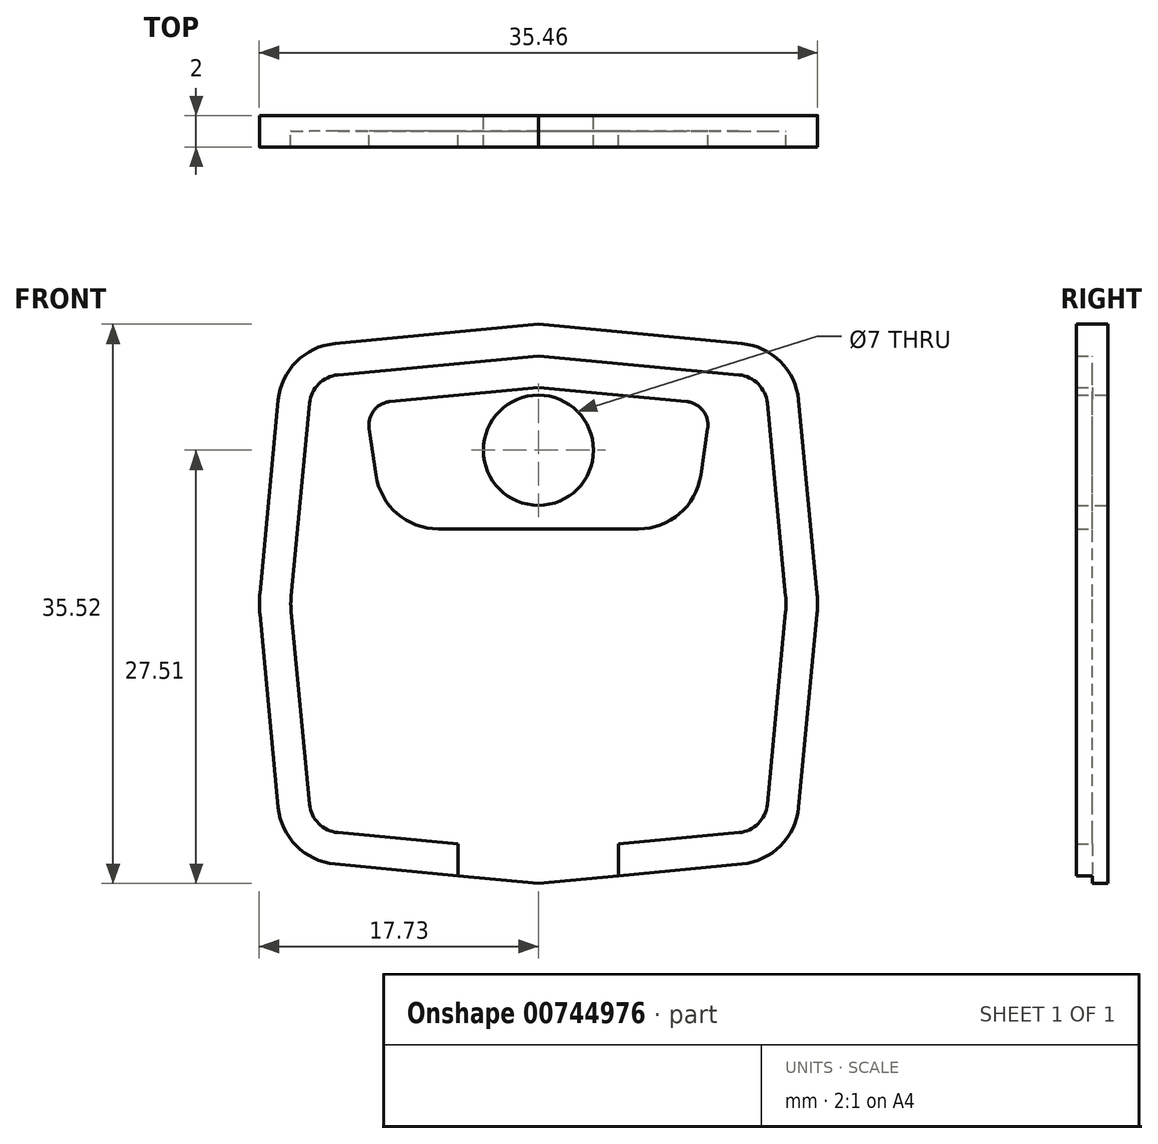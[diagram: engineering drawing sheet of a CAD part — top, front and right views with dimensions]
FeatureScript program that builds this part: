
annotation { "Feature Type Name" : "Feature", "Feature Type Description" : "" }
export const myFeature = defineFeature(function(context is Context, id is Id, definition is map)
    precondition{}
    {
        {
            var Q0;
            Q0=qCreatedBy(makeId("Front.planeOp"),FACE);
            var sketch = newSketch(context, id + "F0", { "sketchPlane" : qUnion([Q0])});
            skLineSegment(sketch, "E0.bottom", {"start": v(0, 31.5) * mm, "end": v(31.5, 31.5) * mm, "construction": true});
            skLineSegment(sketch, "E0.top", {"start": v(0, 0) * mm, "end": v(31.5, 0) * mm, "construction": true});
            skLineSegment(sketch, "E0.left", {"start": v(0, 31.5) * mm, "end": v(0, 0) * mm, "construction": true});
            skLineSegment(sketch, "E0.right", {"start": v(31.5, 31.5) * mm, "end": v(31.5, 0) * mm, "construction": true});
            skLineSegment(sketch, "E1", {"start": v(15.75, 31.5) * mm, "end": v(15.75, 0) * mm, "construction": true});
            skPoint(sketch, "E2", {"position": v(0, 30) * mm});
            skPoint(sketch, "E3", {"position": v(0, 1.5) * mm});
            skPoint(sketch, "E4", {"position": v(15.75, 20.5) * mm});
            skPoint(sketch, "E5", {"position": v(1.5, 31.5) * mm});
            skPoint(sketch, "E6", {"position": v(1.5, 0) * mm});
            skPoint(sketch, "E7", {"position": v(0, 15.75) * mm});
            skLineSegment(sketch, "E8", {"start": v(1.5, 31.5) * mm, "end": v(0, 15.75) * mm, "construction": true});
            skLineSegment(sketch, "E9", {"start": v(1.5, 0) * mm, "end": v(0, 15.75) * mm, "construction": true});
            skLineSegment(sketch, "E10", {"start": v(0, 30) * mm, "end": v(15.75, 31.5) * mm, "construction": true});
            skLineSegment(sketch, "E11", {"start": v(0, 1.5) * mm, "end": v(15.75, 0) * mm, "construction": true});
            skLineSegment(sketch, "E12", {"start": v(15.75, 20.5) * mm, "end": v(0, 20.5) * mm, "construction": true});
            skLineSegment(sketch, "E13", {"start": v(-1.54, 27.84) * mm, "end": v(18.15, 29.72) * mm, "construction": true});
            skLineSegment(sketch, "E14", {"start": v(5, 26.88) * mm, "end": v(5.44, 23.91) * mm});
            skLineSegment(sketch, "E15", {"start": v(6.34, 28.6) * mm, "end": v(15.75, 29.5) * mm});
            skLineSegment(sketch, "E16", {"start": v(15.75, 20.5) * mm, "end": v(9.4, 20.5) * mm});
            skArc(sketch, "E17", {"start": v(6.34, 28.6) * mm, "mid": v(5.3, 28.03) * mm, "end": v(5, 26.88) * mm});
            skArc(sketch, "E18", {"start": v(5.44, 23.91) * mm, "mid": v(6.78, 21.47) * mm, "end": v(9.4, 20.5) * mm});
            skLineSegment(sketch, "E19", {"start": v(15.75, 31.5) * mm, "end": v(3.01, 30.29) * mm});
            skLineSegment(sketch, "E20", {"start": v(1.21, 28.49) * mm, "end": v(0.05, 16.22) * mm, "construction": true});
            skLineSegment(sketch, "E21", {"start": v(0.05, 15.28) * mm, "end": v(1.21, 3.01) * mm});
            skLineSegment(sketch, "E22", {"start": v(3.01, 1.21) * mm, "end": v(15.75, 0) * mm});
            skArc(sketch, "E23", {"start": v(3.01, 30.29) * mm, "mid": v(1.79, 29.71) * mm, "end": v(1.21, 28.49) * mm});
            skArc(sketch, "E24", {"start": v(0.05, 16.22) * mm, "mid": v(0.02, 15.75) * mm, "end": v(0.05, 15.28) * mm});
            skArc(sketch, "E25", {"start": v(1.21, 3.01) * mm, "mid": v(1.79, 1.79) * mm, "end": v(3.01, 1.21) * mm});
            skLineSegment(sketch, "E26", {"start": v(1.21, 28.49) * mm, "end": v(0.05, 16.22) * mm});
            skArc(sketch, "E27.MirrorCS", {"start": v(28.49, 30.29) * mm, "mid": v(29.71, 29.71) * mm, "end": v(30.29, 28.49) * mm});
            skArc(sketch, "E28.MirrorCS", {"start": v(25.16, 28.6) * mm, "mid": v(26.2, 28.03) * mm, "end": v(26.5, 26.88) * mm});
            skArc(sketch, "E29.MirrorCS", {"start": v(26.06, 23.91) * mm, "mid": v(24.72, 21.47) * mm, "end": v(22.1, 20.5) * mm});
            skArc(sketch, "E30.MirrorCS", {"start": v(30.29, 3.01) * mm, "mid": v(29.71, 1.79) * mm, "end": v(28.49, 1.21) * mm});
            skArc(sketch, "E31.MirrorCS", {"start": v(31.45, 16.22) * mm, "mid": v(31.48, 15.75) * mm, "end": v(31.45, 15.28) * mm});
            skLineSegment(sketch, "E32.MirrorCS", {"start": v(26.5, 26.88) * mm, "end": v(26.06, 23.91) * mm});
            skLineSegment(sketch, "E33.MirrorCS", {"start": v(28.49, 1.21) * mm, "end": v(15.75, 0) * mm});
            skLineSegment(sketch, "E34.MirrorCS", {"start": v(30.29, 28.49) * mm, "end": v(31.45, 16.22) * mm});
            skLineSegment(sketch, "E35.MirrorCS", {"start": v(31.45, 15.28) * mm, "end": v(30.29, 3.01) * mm});
            skLineSegment(sketch, "E36.MirrorCS", {"start": v(15.75, 31.5) * mm, "end": v(28.49, 30.29) * mm});
            skLineSegment(sketch, "E37.MirrorCS", {"start": v(25.16, 28.6) * mm, "end": v(15.75, 29.5) * mm});
            skLineSegment(sketch, "E38.MirrorCS", {"start": v(15.75, 20.5) * mm, "end": v(22.1, 20.5) * mm});
            skCircle(sketch, "E39", {"center": v(15.75, 25.5) * mm, "radius": 3.5 * mm});
            skLineSegment(sketch, "E40.0", {"start": v(28.68, -0.78) * mm, "end": v(15.75, -2) * mm});
            skArc(sketch, "E41.0", {"start": v(32.28, 2.82) * mm, "mid": v(31.12, 0.38) * mm, "end": v(28.68, -0.78) * mm});
            skLineSegment(sketch, "E42.0", {"start": v(33.45, 15.09) * mm, "end": v(32.28, 2.82) * mm});
            skArc(sketch, "E43.0", {"start": v(33.45, 16.41) * mm, "mid": v(33.48, 15.75) * mm, "end": v(33.45, 15.09) * mm});
            skLineSegment(sketch, "E44.0", {"start": v(32.28, 28.68) * mm, "end": v(33.45, 16.41) * mm});
            skArc(sketch, "E45.0", {"start": v(28.68, 32.28) * mm, "mid": v(31.12, 31.12) * mm, "end": v(32.28, 28.68) * mm});
            skLineSegment(sketch, "E46.0", {"start": v(15.75, 33.5) * mm, "end": v(28.68, 32.28) * mm});
            skLineSegment(sketch, "E47.MirrorCS", {"start": v(15.75, 33.5) * mm, "end": v(2.82, 32.28) * mm});
            skArc(sketch, "E48.MirrorCS", {"start": v(2.82, 32.28) * mm, "mid": v(0.38, 31.12) * mm, "end": v(-0.78, 28.68) * mm});
            skLineSegment(sketch, "E49.MirrorCS", {"start": v(-0.78, 28.68) * mm, "end": v(-1.95, 16.41) * mm});
            skArc(sketch, "E50.MirrorCS", {"start": v(-1.95, 16.41) * mm, "mid": v(-1.98, 15.75) * mm, "end": v(-1.95, 15.09) * mm});
            skLineSegment(sketch, "E51.MirrorCS", {"start": v(-1.95, 15.09) * mm, "end": v(-0.78, 2.82) * mm});
            skArc(sketch, "E52.MirrorCS", {"start": v(-0.78, 2.82) * mm, "mid": v(0.38, 0.38) * mm, "end": v(2.82, -0.78) * mm});
            skLineSegment(sketch, "E53.MirrorCS", {"start": v(2.82, -0.78) * mm, "end": v(15.75, -2) * mm});
            skLineSegment(sketch, "E54.left", {"start": v(10.65, -1.52) * mm, "end": v(10.65, 0.49) * mm});
            skLineSegment(sketch, "E54.right", {"start": v(20.85, -1.52) * mm, "end": v(20.85, 0.49) * mm});
            skSolve(sketch);
        }
        {
            var Q0;
            Q0=makeQuery(id+"F0.imprint","IMPRINT",FACE,{"disambiguationData":[TD([[makeQuery(id+"F0.imprint","IMPRINT",EDGE,{"derivedFrom":sQuery(id+"F0.wireOp",EDGE,"E19")}),-1.0]])]});
            var Q1;
            Q1=makeQuery(id+"F0.imprint","IMPRINT",FACE,{"disambiguationData":[TD([[makeQuery(id+"F0.imprint","IMPRINT",EDGE,{"derivedFrom":sQuery(id+"F0.wireOp",EDGE,"E14")}),-1.0]])]});
            var Q2;
            Q2=makeQuery(id+"F0.imprint","IMPRINT",FACE,{"disambiguationData":[TD([[makeQuery(id+"F0.imprint","IMPRINT",EDGE,{"derivedFrom":sQuery(id+"F0.wireOp",EDGE,"E14")}),1.0]])]});
            var Q3;
            {var subQ3=sQuery(id+"F0.wireOp",EDGE,"E54.left");Q3=makeQuery(id+"F0.imprint","IMPRINT",FACE,{"disambiguationData":[TD([[makeQuery(id+"F0.imprint","IMPRINT",EDGE,{"derivedFrom":subQ3}),-1.0]])]});}
            extrude(context, id + "F1", {"entities" : qUnion([Q0, Q1, Q2, Q3]), "depth" : 1 * mm, "offsetDistance" : 25 * mm});
        }
        {
            var Q0;
            Q0=makeQuery(id+"F0.imprint","IMPRINT",FACE,{"disambiguationData":[TD([[makeQuery(id+"F0.imprint","IMPRINT",EDGE,{"derivedFrom":sQuery(id+"F0.wireOp",EDGE,"E14")}),1.0]])]});
            var Q1;
            Q1=makeQuery(id+"F0.imprint","IMPRINT",FACE,{"disambiguationData":[TD([[makeQuery(id+"F0.imprint","IMPRINT",EDGE,{"derivedFrom":sQuery(id+"F0.wireOp",EDGE,"E19")}),-1.0]])]});
            extrude(context, id + "F2", {"entities" : qUnion([Q0, Q1]), "operationType" : NewBodyOperationType.ADD, "depth" : 2 * mm, "offsetDistance" : 25 * mm});
        }
    });
